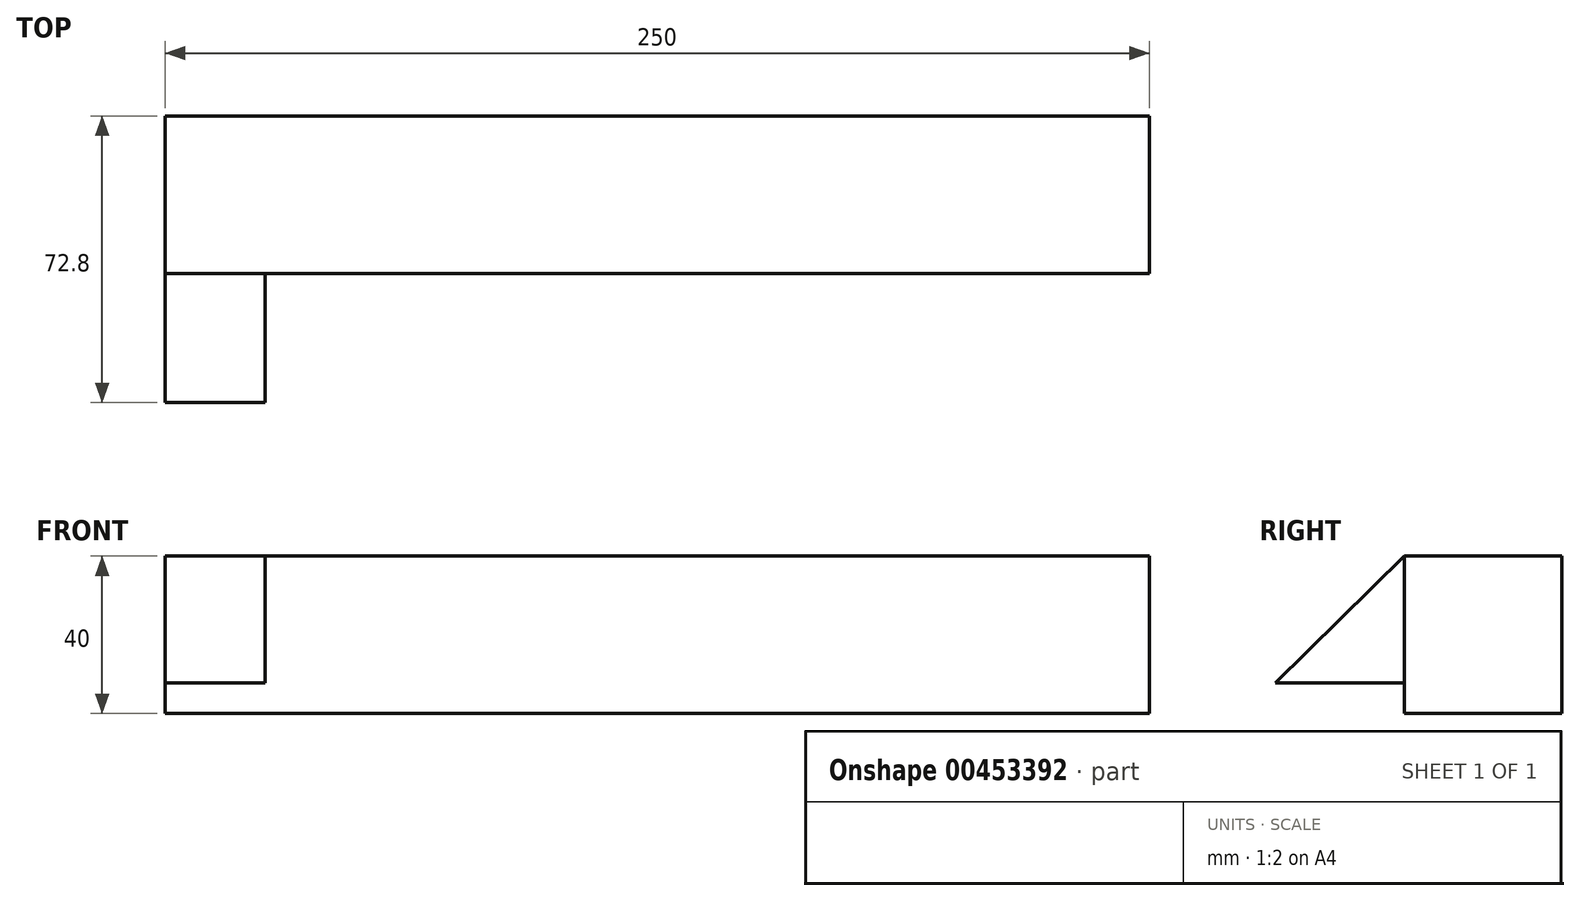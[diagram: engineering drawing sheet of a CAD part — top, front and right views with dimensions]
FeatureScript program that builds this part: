
annotation { "Feature Type Name" : "Feature", "Feature Type Description" : "" }
export const myFeature = defineFeature(function(context is Context, id is Id, definition is map)
    precondition{}
    {
        {
            var Q0;
            Q0=qCreatedBy(makeId("Front.planeOp"),FACE);
            var sketch = newSketch(context, id + "F0", { "sketchPlane" : qUnion([Q0])});
            skLineSegment(sketch, "E0.bottom", {"start": v(-125, 20) * mm, "end": v(125, 20) * mm});
            skLineSegment(sketch, "E0.top", {"start": v(-125, -20) * mm, "end": v(125, -20) * mm});
            skLineSegment(sketch, "E0.left", {"start": v(-125, 20) * mm, "end": v(-125, -20) * mm});
            skLineSegment(sketch, "E0.right", {"start": v(125, 20) * mm, "end": v(125, -20) * mm});
            skSolve(sketch);
        }
        {
            var Q0;
            Q0 = qSketchRegion(id + "F0", true);
            extrude(context, id + "F1", {"entities" : qUnion([Q0]), "depth" : 20 * mm, "hasSecondDirection" : true, "secondDirectionOppositeDirection" : true, "secondDirectionDepth" : 20 * mm});
        }
        {
            var Q0;
            Q0=makeQuery(id+"F1.opExtrude","SWEPT_FACE",FACE,{"disambiguationData":[OSD([sQuery(id+"F0.wireOp",EDGE,"E0.left")])]});
            var sketch = newSketch(context, id + "F2", { "sketchPlane" : qUnion([Q0])});
            skLineSegment(sketch, "E1.top", {"start": v(20, -12.26) * mm, "end": v(52.8, -12.26) * mm});
            skLineSegment(sketch, "E1.left", {"start": v(20, 20) * mm, "end": v(20, -12.26) * mm});
            skLineSegment(sketch, "E2", {"start": v(52.8, -12.26) * mm, "end": v(20, 20) * mm});
            skSolve(sketch);
        }
        {
            var Q0;
            Q0 = qSketchRegion(id + "F2", true);
            extrude(context, id + "F3", {"entities" : qUnion([Q0]), "oppositeDirection" : true, "depth" : 25.4 * mm});
        }
    });
